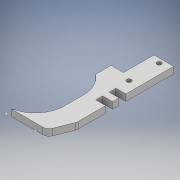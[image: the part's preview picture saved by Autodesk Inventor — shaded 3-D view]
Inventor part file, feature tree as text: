
AUTODESK INVENTOR PART (.ipt)
format: ipt  version: 2017 (Build 210142000, 142)  size: 143,872 bytes
history: native  units: mm
features: sketch x4, extrude x1, hole x1
ambient origin geometry x8: Origin, YZ Plane, XZ Plane, XY Plane, X Axis, Y Axis, Z Axis, Center Point
bodies: Solid1 (feature_tree)
feature tree (6):
  sketch  "Sketch1"  dims[d0=22.0mm d1=90.0deg]
  sketch  "Sketch2"  dims[d2=0.0mm d3=15.0mm]
  extrude  "Extrusion1"  TaperAngle=90.0deg  [1 undecoded]
  hole  "Hole1"  [1 undecoded]
  sketch  "Sketch4"  dims[d5=13.0mm d6=22.0mm d7=12.0mm d8=22.5mm d9=15.0mm d10=90.0mm d11=37.0mm d12=5.0mm d13=12.124057mm d14=5.2mm d15=5.2mm d16=5.0mm d17=7.5mm d18=5.0mm d19=0.0mm d20=23.0mm d21=7.5mm d22=7.5mm d23=3.5mm d24=3.4mm d25=6.0mm d26=4.0mm d27=2.0mm d28=90.0deg d29=8.0mm d30=20.594885mm]
  sketch  "Sketch3"  dims[d4=0.0mm]
note: 2 required parameter values undecoded (feature->parameter linkage not recoverable at this tier; creation-order binding heuristic only, values carry confidence <= 0.55)
